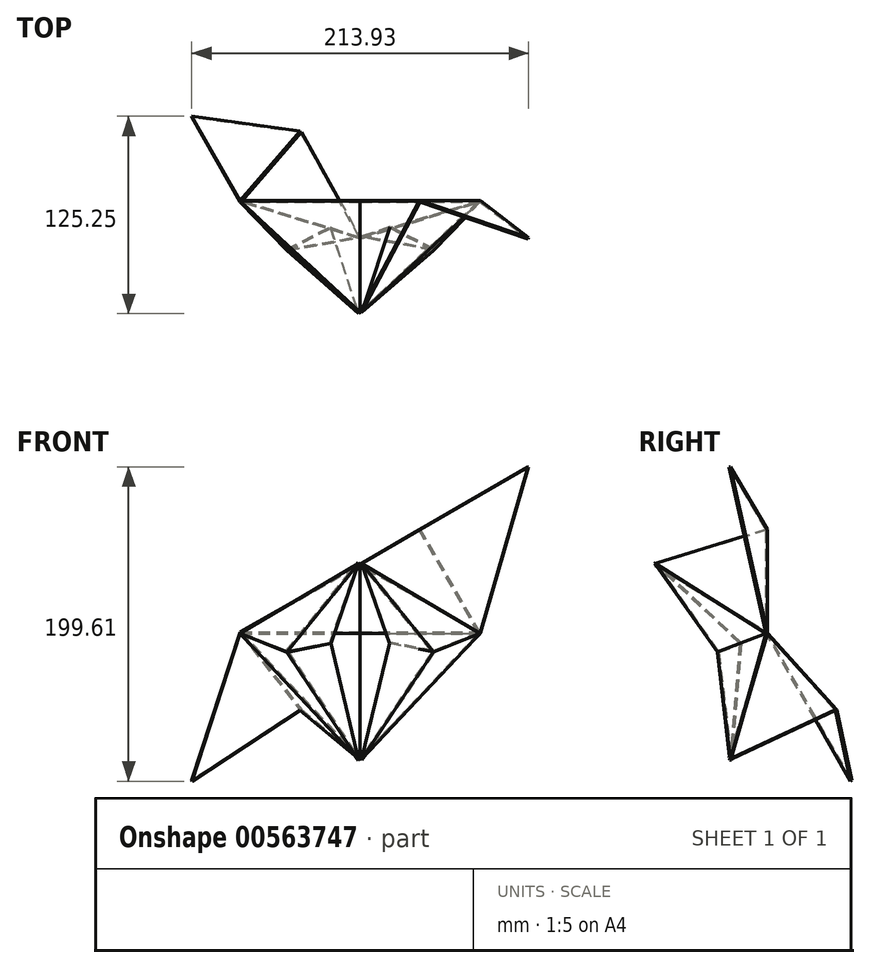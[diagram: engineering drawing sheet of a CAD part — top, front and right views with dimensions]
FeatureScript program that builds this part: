
annotation { "Feature Type Name" : "Feature", "Feature Type Description" : "" }
export const myFeature = defineFeature(function(context is Context, id is Id, definition is map)
    precondition{}
    {
        {
            var Q0;
            Q0=qCreatedBy(makeId("Front.planeOp"),FACE);
            var sketch = newSketch(context, id + "F0", { "sketchPlane" : qUnion([Q0])});
            skLineSegment(sketch, "E0", {"start": v(0, 0) * mm, "end": v(76.2, 0) * mm});
            skLineSegment(sketch, "E1", {"start": v(76.2, 0) * mm, "end": v(152.4, 0) * mm});
            skLineSegment(sketch, "E2", {"start": v(152.4, 0) * mm, "end": v(114.3, 66) * mm});
            skLineSegment(sketch, "E3", {"start": v(0, 0) * mm, "end": v(38.1, 66) * mm});
            skLineSegment(sketch, "E4", {"start": v(38.1, 66) * mm, "end": v(76.2, 131.98) * mm});
            skLineSegment(sketch, "E5", {"start": v(76.2, 131.98) * mm, "end": v(114.3, 66) * mm});
            skLineSegment(sketch, "E6", {"start": v(76.2, 0) * mm, "end": v(76.2, -82.55) * mm});
            skLineSegment(sketch, "E7", {"start": v(38.1, 66) * mm, "end": v(-33.4, 107.27) * mm});
            skLineSegment(sketch, "E8", {"start": v(114.3, 66) * mm, "end": v(185.8, 107.27) * mm});
            skLineSegment(sketch, "E9", {"start": v(-33.4, 107.27) * mm, "end": v(76.2, 131.98) * mm});
            skLineSegment(sketch, "E10", {"start": v(-33.4, 107.27) * mm, "end": v(0, 0) * mm});
            skLineSegment(sketch, "E11", {"start": v(76.2, -82.55) * mm, "end": v(152.4, 0) * mm});
            skLineSegment(sketch, "E12", {"start": v(76.2, -82.55) * mm, "end": v(0, 0) * mm});
            skLineSegment(sketch, "E13", {"start": v(152.4, 0) * mm, "end": v(185.8, 107.27) * mm});
            skLineSegment(sketch, "E14", {"start": v(76.2, 131.98) * mm, "end": v(185.8, 107.27) * mm});
            skLineSegment(sketch, "E15", {"start": v(152.4, 0) * mm, "end": v(189.3, 24.8) * mm});
            skLineSegment(sketch, "E16", {"start": v(189.3, 24.8) * mm, "end": v(185.8, 107.27) * mm});
            skLineSegment(sketch, "E17", {"start": v(152.4, 0) * mm, "end": v(149.38, -44.35) * mm});
            skLineSegment(sketch, "E18", {"start": v(149.38, -44.35) * mm, "end": v(76.2, -82.55) * mm});
            skLineSegment(sketch, "E19", {"start": v(0, 0) * mm, "end": v(3.02, -44.35) * mm});
            skLineSegment(sketch, "E20", {"start": v(3.02, -44.35) * mm, "end": v(76.2, -82.55) * mm});
            skLineSegment(sketch, "E21", {"start": v(0, 0) * mm, "end": v(-36.9, 24.8) * mm});
            skLineSegment(sketch, "E22", {"start": v(-36.9, 24.8) * mm, "end": v(-33.4, 107.27) * mm});
            skLineSegment(sketch, "E23", {"start": v(-33.4, 107.27) * mm, "end": v(36.28, 151.54) * mm});
            skLineSegment(sketch, "E24", {"start": v(36.28, 151.54) * mm, "end": v(76.2, 131.98) * mm});
            skLineSegment(sketch, "E25", {"start": v(76.2, 131.98) * mm, "end": v(116.12, 151.54) * mm});
            skLineSegment(sketch, "E26", {"start": v(116.12, 151.54) * mm, "end": v(185.8, 107.27) * mm});
            skLineSegment(sketch, "E27", {"start": v(149.38, -44.35) * mm, "end": v(152.12, -75.98) * mm});
            skLineSegment(sketch, "E28", {"start": v(152.12, -75.98) * mm, "end": v(76.2, -82.55) * mm});
            skLineSegment(sketch, "E29.MirrorCS", {"start": v(0.28, -75.98) * mm, "end": v(76.2, -82.55) * mm});
            skLineSegment(sketch, "E30.MirrorCS", {"start": v(3.02, -44.35) * mm, "end": v(0.28, -75.98) * mm});
            skLineSegment(sketch, "E31", {"start": v(-36.9, 24.8) * mm, "end": v(-65.66, 38.24) * mm});
            skLineSegment(sketch, "E32", {"start": v(-65.66, 38.24) * mm, "end": v(-33.4, 107.27) * mm});
            skLineSegment(sketch, "E33.MirrorCS", {"start": v(10.26, 169.73) * mm, "end": v(-33.4, 107.27) * mm});
            skLineSegment(sketch, "E34.MirrorCS", {"start": v(36.28, 151.54) * mm, "end": v(10.26, 169.73) * mm});
            skLineSegment(sketch, "E35", {"start": v(116.12, 151.54) * mm, "end": v(142.14, 169.73) * mm});
            skLineSegment(sketch, "E36", {"start": v(142.14, 169.73) * mm, "end": v(185.8, 107.27) * mm});
            skLineSegment(sketch, "E37.MirrorCS", {"start": v(218.06, 38.24) * mm, "end": v(185.8, 107.27) * mm});
            skLineSegment(sketch, "E38.MirrorCS", {"start": v(189.3, 24.8) * mm, "end": v(218.06, 38.24) * mm});
            skText(sketch, "E39", { "text": "angle of 121.5 between three sides of pyramid\nangle of 42 between pyramids (31.5+31.5+42=105)\nangle of 23 of top of star\nangle of 88 of bottom of star\nangle 16.5 of top flap\n", "fontName": "OpenSans-Regular.ttf"});
            skLineSegment(sketch, "E40", {"start": v(76.2, 131.98) * mm, "end": v(76.2, 0) * mm});
            skLineSegment(sketch, "E41", {"start": v(114.3, 66) * mm, "end": v(0, 0) * mm});
            skLineSegment(sketch, "E42", {"start": v(152.4, 0) * mm, "end": v(38.1, 66) * mm});
            skPoint(sketch, "E43", {"position": v(76.2, 44) * mm});
            skPoint(sketch, "E44", {"position": v(76.2, -82.55) * mm});
            skPoint(sketch, "E45", {"position": v(185.8, 107.27) * mm});
            skPoint(sketch, "E46", {"position": v(-33.4, 107.27) * mm});
            skPoint(sketch, "E47", {"position": v(76.2, -44) * mm});
            const initialGuessF0  = {"E39": [0.43458, 0, 1, 0, 0.01522]};
            skSetInitialGuess(sketch, initialGuessF0);
            skSolve(sketch);
        }
        {
            var Q0;
            Q0=makeQuery(id+"F0.imprint","IMPRINT",FACE,{"disambiguationData":[TD([[makeQuery(id+"F0.imprint","IMPRINT",EDGE,{"derivedFrom":sQuery(id+"F0.wireOp",EDGE,"E3")}),1.0]])]});
            var Q1;
            Q1=makeQuery(id+"F0.imprint","IMPRINT",FACE,{"disambiguationData":[TD([[makeQuery(id+"F0.imprint","IMPRINT",EDGE,{"derivedFrom":sQuery(id+"F0.wireOp",EDGE,"E1")}),-1.0]])]});
            var Q2;
            Q2=makeQuery(id+"F0.imprint","IMPRINT",FACE,{"disambiguationData":[TD([[makeQuery(id+"F0.imprint","IMPRINT",EDGE,{"derivedFrom":sQuery(id+"F0.wireOp",EDGE,"E5")}),1.0]])]});
            extrude(context, id + "F1", {"entities" : qUnion([Q0, Q1, Q2]), "depth" : 1.02 * mm, "offsetDistance" : 25.4 * mm});
        }
        {
            var Q0;
            Q0=makeQuery(id+"F0.imprint","IMPRINT",FACE,{"disambiguationData":[TD([[makeQuery(id+"F0.imprint","IMPRINT",EDGE,{"derivedFrom":sQuery(id+"F0.wireOp",EDGE,"E4")}),1.0]])]});
            var Q1;
            Q1=makeQuery(id+"F0.imprint","IMPRINT",FACE,{"disambiguationData":[TD([[makeQuery(id+"F0.imprint","IMPRINT",EDGE,{"derivedFrom":sQuery(id+"F0.wireOp",EDGE,"E0")}),-1.0]])]});
            var Q2;
            Q2=makeQuery(id+"F0.imprint","IMPRINT",FACE,{"disambiguationData":[TD([[makeQuery(id+"F0.imprint","IMPRINT",EDGE,{"derivedFrom":sQuery(id+"F0.wireOp",EDGE,"E2")}),-1.0]])]});
            extrude(context, id + "F2", {"entities" : qUnion([Q0, Q1, Q2]), "depth" : 1.02 * mm, "offsetDistance" : 25.4 * mm});
        }
        {
            var Q0;
            Q0=makeQuery(id+"F0.imprint","IMPRINT",FACE,{"disambiguationData":[TD([[makeQuery(id+"F0.imprint","IMPRINT",EDGE,{"derivedFrom":sQuery(id+"F0.wireOp",EDGE,"E10")}),-1.0]])]});
            var Q1;
            Q1=makeQuery(id+"F0.imprint","IMPRINT",FACE,{"disambiguationData":[TD([[makeQuery(id+"F0.imprint","IMPRINT",EDGE,{"derivedFrom":sQuery(id+"F0.wireOp",EDGE,"E11")}),-1.0]])]});
            var Q2;
            Q2=makeQuery(id+"F0.imprint","IMPRINT",FACE,{"disambiguationData":[TD([[makeQuery(id+"F0.imprint","IMPRINT",EDGE,{"derivedFrom":sQuery(id+"F0.wireOp",EDGE,"E14")}),1.0]])]});
            extrude(context, id + "F3", {"entities" : qUnion([Q0, Q1, Q2]), "depth" : 1.02 * mm, "offsetDistance" : 25.4 * mm});
        }
        {
            var Q0;
            Q0=makeQuery(id+"F0.imprint","IMPRINT",FACE,{"disambiguationData":[TD([[makeQuery(id+"F0.imprint","IMPRINT",EDGE,{"derivedFrom":sQuery(id+"F0.wireOp",EDGE,"E9")}),1.0]])]});
            var Q1;
            Q1=makeQuery(id+"F0.imprint","IMPRINT",FACE,{"disambiguationData":[TD([[makeQuery(id+"F0.imprint","IMPRINT",EDGE,{"derivedFrom":sQuery(id+"F0.wireOp",EDGE,"E12")}),1.0]])]});
            var Q2;
            Q2=makeQuery(id+"F0.imprint","IMPRINT",FACE,{"disambiguationData":[TD([[makeQuery(id+"F0.imprint","IMPRINT",EDGE,{"derivedFrom":sQuery(id+"F0.wireOp",EDGE,"E13")}),-1.0]])]});
            extrude(context, id + "F4", {"entities" : qUnion([Q0, Q1, Q2]), "depth" : 1.02 * mm, "offsetDistance" : 25.4 * mm});
        }
        {
            var Q0;
            Q0=makeQuery(id+"F0.imprint","IMPRINT",FACE,{"disambiguationData":[TD([[makeQuery(id+"F0.imprint","IMPRINT",EDGE,{"derivedFrom":sQuery(id+"F0.wireOp",EDGE,"E22")}),1.0]])]});
            var Q1;
            Q1=makeQuery(id+"F0.imprint","IMPRINT",FACE,{"disambiguationData":[TD([[makeQuery(id+"F0.imprint","IMPRINT",EDGE,{"derivedFrom":sQuery(id+"F0.wireOp",EDGE,"E18")}),1.0]])]});
            var Q2;
            Q2=makeQuery(id+"F0.imprint","IMPRINT",FACE,{"disambiguationData":[TD([[makeQuery(id+"F0.imprint","IMPRINT",EDGE,{"derivedFrom":sQuery(id+"F0.wireOp",EDGE,"E26")}),1.0]])]});
            extrude(context, id + "F5", {"entities" : qUnion([Q0, Q1, Q2]), "depth" : 1.02 * mm, "offsetDistance" : 25.4 * mm});
        }
        {
            var Q0;
            Q0=makeQuery(id+"F0.imprint","IMPRINT",FACE,{"disambiguationData":[TD([[makeQuery(id+"F0.imprint","IMPRINT",EDGE,{"derivedFrom":sQuery(id+"F0.wireOp",EDGE,"E23")}),1.0]])]});
            var Q1;
            Q1=makeQuery(id+"F0.imprint","IMPRINT",FACE,{"disambiguationData":[TD([[makeQuery(id+"F0.imprint","IMPRINT",EDGE,{"derivedFrom":sQuery(id+"F0.wireOp",EDGE,"E20")}),-1.0]])]});
            var Q2;
            Q2=makeQuery(id+"F0.imprint","IMPRINT",FACE,{"disambiguationData":[TD([[makeQuery(id+"F0.imprint","IMPRINT",EDGE,{"derivedFrom":sQuery(id+"F0.wireOp",EDGE,"E16")}),-1.0]])]});
            extrude(context, id + "F6", {"entities" : qUnion([Q0, Q1, Q2]), "depth" : 1.02 * mm, "offsetDistance" : 25.4 * mm});
        }
        {
            var Q0;
            Q0=makeQuery(id+"F2.opExtrude","SWEPT_BODY",BODY,{"disambiguationData":[OSD([sQuery(id+"F0.wireOp",EDGE,"E0"),sQuery(id+"F0.wireOp",EDGE,"E6"),sQuery(id+"F0.wireOp",EDGE,"E12")])]});
            var Q1;
            Q1=makeQuery(id+"F4.opExtrude","SWEPT_BODY",BODY,{"disambiguationData":[OSD([sQuery(id+"F0.wireOp",EDGE,"E12"),sQuery(id+"F0.wireOp",EDGE,"E19"),sQuery(id+"F0.wireOp",EDGE,"E20")])]});
            var Q2;
            Q2=makeQuery(id+"F6.opExtrude","SWEPT_BODY",BODY,{"disambiguationData":[OSD([sQuery(id+"F0.wireOp",EDGE,"E20"),sQuery(id+"F0.wireOp",EDGE,"E29.MirrorCS"),sQuery(id+"F0.wireOp",EDGE,"E30.MirrorCS")])]});
            var Q3;
            Q3=makeQuery(id+"F5.opExtrude","SWEPT_BODY",BODY,{"disambiguationData":[OSD([sQuery(id+"F0.wireOp",EDGE,"E18"),sQuery(id+"F0.wireOp",EDGE,"E27"),sQuery(id+"F0.wireOp",EDGE,"E28")])]});
            var Q4;
            Q4=makeQuery(id+"F3.opExtrude","SWEPT_BODY",BODY,{"disambiguationData":[OSD([sQuery(id+"F0.wireOp",EDGE,"E11"),sQuery(id+"F0.wireOp",EDGE,"E17"),sQuery(id+"F0.wireOp",EDGE,"E18")])]});
            var Q5;
            Q5=makeQuery(id+"F1.opExtrude","SWEPT_BODY",BODY,{"disambiguationData":[OSD([sQuery(id+"F0.wireOp",EDGE,"E1"),sQuery(id+"F0.wireOp",EDGE,"E6"),sQuery(id+"F0.wireOp",EDGE,"E11")])]});
            var Q6;
            Q6=sQuery(id+"F0.wireOp",EDGE,"E1");
            transform(context, id + "F7", {"entities" : qUnion([Q0, Q1, Q2, Q3, Q4, Q5]), "transformType" : TransformType.ROTATION, "transformAxis" : qUnion([Q6]), "angle" : 121.5 * degree, "oppositeDirection" : true, "makeCopy" : false});
        }
        {
            var Q0;
            Q0=makeQuery(id+"F1.opExtrude","SWEPT_BODY",BODY,{"disambiguationData":[OSD([sQuery(id+"F0.wireOp",EDGE,"E3"),sQuery(id+"F0.wireOp",EDGE,"E7"),sQuery(id+"F0.wireOp",EDGE,"E10")])]});
            var Q1;
            Q1=makeQuery(id+"F3.opExtrude","SWEPT_BODY",BODY,{"disambiguationData":[OSD([sQuery(id+"F0.wireOp",EDGE,"E10"),sQuery(id+"F0.wireOp",EDGE,"E21"),sQuery(id+"F0.wireOp",EDGE,"E22")])]});
            var Q2;
            Q2=makeQuery(id+"F5.opExtrude","SWEPT_BODY",BODY,{"disambiguationData":[OSD([sQuery(id+"F0.wireOp",EDGE,"E22"),sQuery(id+"F0.wireOp",EDGE,"E31"),sQuery(id+"F0.wireOp",EDGE,"E32")])]});
            var Q3;
            Q3=makeQuery(id+"F6.opExtrude","SWEPT_BODY",BODY,{"disambiguationData":[OSD([sQuery(id+"F0.wireOp",EDGE,"E23"),sQuery(id+"F0.wireOp",EDGE,"E33.MirrorCS"),sQuery(id+"F0.wireOp",EDGE,"E34.MirrorCS")])]});
            var Q4;
            Q4=makeQuery(id+"F4.opExtrude","SWEPT_BODY",BODY,{"disambiguationData":[OSD([sQuery(id+"F0.wireOp",EDGE,"E9"),sQuery(id+"F0.wireOp",EDGE,"E23"),sQuery(id+"F0.wireOp",EDGE,"E24")])]});
            var Q5;
            Q5=makeQuery(id+"F2.opExtrude","SWEPT_BODY",BODY,{"disambiguationData":[OSD([sQuery(id+"F0.wireOp",EDGE,"E4"),sQuery(id+"F0.wireOp",EDGE,"E7"),sQuery(id+"F0.wireOp",EDGE,"E9")])]});
            var Q6;
            Q6=sQuery(id+"F0.wireOp",EDGE,"E3");
            transform(context, id + "F8", {"entities" : qUnion([Q0, Q1, Q2, Q3, Q4, Q5]), "transformType" : TransformType.ROTATION, "transformAxis" : qUnion([Q6]), "angle" : 121.5 * degree, "makeCopy" : false});
        }
        {
            var Q0;
            Q0=makeQuery(id+"F2.opExtrude","SWEPT_BODY",BODY,{"disambiguationData":[OSD([sQuery(id+"F0.wireOp",EDGE,"E2"),sQuery(id+"F0.wireOp",EDGE,"E8"),sQuery(id+"F0.wireOp",EDGE,"E13")])]});
            var Q1;
            Q1=makeQuery(id+"F1.opExtrude","SWEPT_BODY",BODY,{"disambiguationData":[OSD([sQuery(id+"F0.wireOp",EDGE,"E5"),sQuery(id+"F0.wireOp",EDGE,"E8"),sQuery(id+"F0.wireOp",EDGE,"E14")])]});
            var Q2;
            Q2=makeQuery(id+"F3.opExtrude","SWEPT_BODY",BODY,{"disambiguationData":[OSD([sQuery(id+"F0.wireOp",EDGE,"E14"),sQuery(id+"F0.wireOp",EDGE,"E25"),sQuery(id+"F0.wireOp",EDGE,"E26")])]});
            var Q3;
            Q3=makeQuery(id+"F5.opExtrude","SWEPT_BODY",BODY,{"disambiguationData":[OSD([sQuery(id+"F0.wireOp",EDGE,"E26"),sQuery(id+"F0.wireOp",EDGE,"E35"),sQuery(id+"F0.wireOp",EDGE,"E36")])]});
            var Q4;
            Q4=makeQuery(id+"F6.opExtrude","SWEPT_BODY",BODY,{"disambiguationData":[OSD([sQuery(id+"F0.wireOp",EDGE,"E16"),sQuery(id+"F0.wireOp",EDGE,"E37.MirrorCS"),sQuery(id+"F0.wireOp",EDGE,"E38.MirrorCS")])]});
            var Q5;
            Q5=makeQuery(id+"F4.opExtrude","SWEPT_BODY",BODY,{"disambiguationData":[OSD([sQuery(id+"F0.wireOp",EDGE,"E13"),sQuery(id+"F0.wireOp",EDGE,"E15"),sQuery(id+"F0.wireOp",EDGE,"E16")])]});
            var Q6;
            Q6=sQuery(id+"F0.wireOp",EDGE,"E5");
            transform(context, id + "F9", {"entities" : qUnion([Q0, Q1, Q2, Q3, Q4, Q5]), "transformType" : TransformType.ROTATION, "transformAxis" : qUnion([Q6]), "angle" : 121.5 * degree, "makeCopy" : false});
        }
        {
            var Q0;
            Q0=makeQuery(id+"F4.opExtrude","SWEPT_BODY",BODY,{"disambiguationData":[OSD([sQuery(id+"F0.wireOp",EDGE,"E13"),sQuery(id+"F0.wireOp",EDGE,"E15"),sQuery(id+"F0.wireOp",EDGE,"E16")])]});
            var Q1;
            Q1=makeQuery(id+"F6.opExtrude","SWEPT_BODY",BODY,{"disambiguationData":[OSD([sQuery(id+"F0.wireOp",EDGE,"E16"),sQuery(id+"F0.wireOp",EDGE,"E37.MirrorCS"),sQuery(id+"F0.wireOp",EDGE,"E38.MirrorCS")])]});
            var Q2;
            Q2=makeQuery(id+"F2.opExtrude","CAP_EDGE",EDGE,{"disambiguationData":[OSD([sQuery(id+"F0.wireOp",EDGE,"E13")])],"isStart":true});
            transform(context, id + "F10", {"entities" : qUnion([Q0, Q1]), "transformType" : TransformType.ROTATION, "transformAxis" : qUnion([Q2]), "angle" : 23 * degree, "oppositeDirection" : true, "makeCopy" : false});
        }
        {
            var Q0;
            Q0=makeQuery(id+"F3.opExtrude","SWEPT_BODY",BODY,{"disambiguationData":[OSD([sQuery(id+"F0.wireOp",EDGE,"E11"),sQuery(id+"F0.wireOp",EDGE,"E17"),sQuery(id+"F0.wireOp",EDGE,"E18")])]});
            var Q1;
            Q1=makeQuery(id+"F5.opExtrude","SWEPT_BODY",BODY,{"disambiguationData":[OSD([sQuery(id+"F0.wireOp",EDGE,"E18"),sQuery(id+"F0.wireOp",EDGE,"E27"),sQuery(id+"F0.wireOp",EDGE,"E28")])]});
            var Q2;
            Q2=makeQuery(id+"F1.opExtrude","CAP_EDGE",EDGE,{"disambiguationData":[OSD([sQuery(id+"F0.wireOp",EDGE,"E11")])],"isStart":true});
            transform(context, id + "F11", {"entities" : qUnion([Q0, Q1]), "transformType" : TransformType.ROTATION, "transformAxis" : qUnion([Q2]), "angle" : 23 * degree, "oppositeDirection" : true, "makeCopy" : false});
        }
        {
            var Q0;
            Q0=makeQuery(id+"F4.opExtrude","SWEPT_BODY",BODY,{"disambiguationData":[OSD([sQuery(id+"F0.wireOp",EDGE,"E9"),sQuery(id+"F0.wireOp",EDGE,"E23"),sQuery(id+"F0.wireOp",EDGE,"E24")])]});
            var Q1;
            Q1=makeQuery(id+"F6.opExtrude","SWEPT_BODY",BODY,{"disambiguationData":[OSD([sQuery(id+"F0.wireOp",EDGE,"E23"),sQuery(id+"F0.wireOp",EDGE,"E33.MirrorCS"),sQuery(id+"F0.wireOp",EDGE,"E34.MirrorCS")])]});
            var Q2;
            Q2=makeQuery(id+"F2.opExtrude","CAP_EDGE",EDGE,{"disambiguationData":[OSD([sQuery(id+"F0.wireOp",EDGE,"E9")])],"isStart":true});
            transform(context, id + "F12", {"entities" : qUnion([Q0, Q1]), "transformType" : TransformType.ROTATION, "transformAxis" : qUnion([Q2]), "angle" : 23 * degree, "makeCopy" : false});
        }
        {
            var Q0;
            Q0=makeQuery(id+"F3.opExtrude","SWEPT_BODY",BODY,{"disambiguationData":[OSD([sQuery(id+"F0.wireOp",EDGE,"E14"),sQuery(id+"F0.wireOp",EDGE,"E25"),sQuery(id+"F0.wireOp",EDGE,"E26")])]});
            var Q1;
            Q1=makeQuery(id+"F5.opExtrude","SWEPT_BODY",BODY,{"disambiguationData":[OSD([sQuery(id+"F0.wireOp",EDGE,"E26"),sQuery(id+"F0.wireOp",EDGE,"E35"),sQuery(id+"F0.wireOp",EDGE,"E36")])]});
            var Q2;
            Q2=makeQuery(id+"F1.opExtrude","CAP_EDGE",EDGE,{"disambiguationData":[OSD([sQuery(id+"F0.wireOp",EDGE,"E14")])],"isStart":true});
            transform(context, id + "F13", {"entities" : qUnion([Q0, Q1]), "transformType" : TransformType.ROTATION, "transformAxis" : qUnion([Q2]), "angle" : 23 * degree, "makeCopy" : false});
        }
        {
            var Q0;
            Q0=makeQuery(id+"F4.opExtrude","SWEPT_BODY",BODY,{"disambiguationData":[OSD([sQuery(id+"F0.wireOp",EDGE,"E12"),sQuery(id+"F0.wireOp",EDGE,"E19"),sQuery(id+"F0.wireOp",EDGE,"E20")])]});
            var Q1;
            Q1=makeQuery(id+"F6.opExtrude","SWEPT_BODY",BODY,{"disambiguationData":[OSD([sQuery(id+"F0.wireOp",EDGE,"E20"),sQuery(id+"F0.wireOp",EDGE,"E29.MirrorCS"),sQuery(id+"F0.wireOp",EDGE,"E30.MirrorCS")])]});
            var Q2;
            Q2=makeQuery(id+"F1.opExtrude","CAP_EDGE",EDGE,{"disambiguationData":[OSD([sQuery(id+"F0.wireOp",EDGE,"E10")])],"isStart":true});
            transform(context, id + "F14", {"entities" : qUnion([Q0, Q1]), "transformType" : TransformType.ROTATION, "transformAxis" : qUnion([Q2]), "angle" : 23 * degree, "makeCopy" : false});
        }
        {
            var Q0;
            Q0=makeQuery(id+"F3.opExtrude","SWEPT_BODY",BODY,{"disambiguationData":[OSD([sQuery(id+"F0.wireOp",EDGE,"E10"),sQuery(id+"F0.wireOp",EDGE,"E21"),sQuery(id+"F0.wireOp",EDGE,"E22")])]});
            var Q1;
            Q1=makeQuery(id+"F5.opExtrude","SWEPT_BODY",BODY,{"disambiguationData":[OSD([sQuery(id+"F0.wireOp",EDGE,"E22"),sQuery(id+"F0.wireOp",EDGE,"E31"),sQuery(id+"F0.wireOp",EDGE,"E32")])]});
            var Q2;
            Q2=makeQuery(id+"F4.opExtrude","CAP_EDGE",EDGE,{"disambiguationData":[OSD([sQuery(id+"F0.wireOp",EDGE,"E12")])],"isStart":true});
            transform(context, id + "F15", {"entities" : qUnion([Q0, Q1]), "transformType" : TransformType.ROTATION, "transformAxis" : qUnion([Q2]), "angle" : 23 * degree, "oppositeDirection" : true, "makeCopy" : false});
        }
        {
            var Q0;
            Q0=makeQuery(id+"F6.opExtrude","SWEPT_BODY",BODY,{"disambiguationData":[OSD([sQuery(id+"F0.wireOp",EDGE,"E23"),sQuery(id+"F0.wireOp",EDGE,"E33.MirrorCS"),sQuery(id+"F0.wireOp",EDGE,"E34.MirrorCS")])]});
            var Q1;
            Q1=makeQuery(id+"F4.opExtrude","CAP_EDGE",EDGE,{"disambiguationData":[OSD([sQuery(id+"F0.wireOp",EDGE,"E23")])],"isStart":true});
            transform(context, id + "F16", {"entities" : qUnion([Q0]), "transformType" : TransformType.ROTATION, "transformAxis" : qUnion([Q1]), "angle" : 88 * degree, "makeCopy" : false});
        }
        {
            var Q0;
            Q0=makeQuery(id+"F5.opExtrude","SWEPT_BODY",BODY,{"disambiguationData":[OSD([sQuery(id+"F0.wireOp",EDGE,"E18"),sQuery(id+"F0.wireOp",EDGE,"E27"),sQuery(id+"F0.wireOp",EDGE,"E28")])]});
            var Q1;
            Q1=makeQuery(id+"F3.opExtrude","CAP_EDGE",EDGE,{"disambiguationData":[OSD([sQuery(id+"F0.wireOp",EDGE,"E18")])],"isStart":true});
            transform(context, id + "F17", {"entities" : qUnion([Q0]), "transformType" : TransformType.ROTATION, "transformAxis" : qUnion([Q1]), "angle" : 88 * degree, "makeCopy" : false});
        }
        {
            var Q0;
            Q0=makeQuery(id+"F6.opExtrude","SWEPT_BODY",BODY,{"disambiguationData":[OSD([sQuery(id+"F0.wireOp",EDGE,"E16"),sQuery(id+"F0.wireOp",EDGE,"E37.MirrorCS"),sQuery(id+"F0.wireOp",EDGE,"E38.MirrorCS")])]});
            var Q1;
            Q1=makeQuery(id+"F4.opExtrude","CAP_EDGE",EDGE,{"disambiguationData":[OSD([sQuery(id+"F0.wireOp",EDGE,"E16")])],"isStart":true});
            transform(context, id + "F18", {"entities" : qUnion([Q0]), "transformType" : TransformType.ROTATION, "transformAxis" : qUnion([Q1]), "angle" : 88 * degree, "oppositeDirection" : true, "makeCopy" : false});
        }
        {
            var Q0;
            Q0=makeQuery(id+"F5.opExtrude","SWEPT_BODY",BODY,{"disambiguationData":[OSD([sQuery(id+"F0.wireOp",EDGE,"E22"),sQuery(id+"F0.wireOp",EDGE,"E31"),sQuery(id+"F0.wireOp",EDGE,"E32")])]});
            var Q1;
            Q1=makeQuery(id+"F3.opExtrude","CAP_EDGE",EDGE,{"disambiguationData":[OSD([sQuery(id+"F0.wireOp",EDGE,"E22")])],"isStart":true});
            transform(context, id + "F19", {"entities" : qUnion([Q0]), "transformType" : TransformType.ROTATION, "transformAxis" : qUnion([Q1]), "angle" : 88 * degree, "makeCopy" : false});
        }
        {
            var Q0;
            Q0=makeQuery(id+"F6.opExtrude","SWEPT_BODY",BODY,{"disambiguationData":[OSD([sQuery(id+"F0.wireOp",EDGE,"E20"),sQuery(id+"F0.wireOp",EDGE,"E29.MirrorCS"),sQuery(id+"F0.wireOp",EDGE,"E30.MirrorCS")])]});
            var Q1;
            Q1=makeQuery(id+"F4.opExtrude","CAP_EDGE",EDGE,{"disambiguationData":[OSD([sQuery(id+"F0.wireOp",EDGE,"E20")])],"isStart":true});
            transform(context, id + "F20", {"entities" : qUnion([Q0]), "transformType" : TransformType.ROTATION, "transformAxis" : qUnion([Q1]), "angle" : 88 * degree, "oppositeDirection" : true, "makeCopy" : false});
        }
        {
            var Q0;
            Q0=makeQuery(id+"F5.opExtrude","SWEPT_BODY",BODY,{"disambiguationData":[OSD([sQuery(id+"F0.wireOp",EDGE,"E26"),sQuery(id+"F0.wireOp",EDGE,"E35"),sQuery(id+"F0.wireOp",EDGE,"E36")])]});
            var Q1;
            Q1=makeQuery(id+"F3.opExtrude","CAP_EDGE",EDGE,{"disambiguationData":[OSD([sQuery(id+"F0.wireOp",EDGE,"E26")])],"isStart":true});
            transform(context, id + "F21", {"entities" : qUnion([Q0]), "transformType" : TransformType.ROTATION, "transformAxis" : qUnion([Q1]), "angle" : 88 * degree, "makeCopy" : false});
        }
        {
            var Q0;
            Q0=makeQuery(id+"F5.opExtrude","SWEPT_BODY",BODY,{"disambiguationData":[OSD([sQuery(id+"F0.wireOp",EDGE,"E22"),sQuery(id+"F0.wireOp",EDGE,"E31"),sQuery(id+"F0.wireOp",EDGE,"E32")])]});
            var Q1;
            Q1=makeQuery(id+"F5.opExtrude","SWEPT_BODY",BODY,{"disambiguationData":[OSD([sQuery(id+"F0.wireOp",EDGE,"E18"),sQuery(id+"F0.wireOp",EDGE,"E27"),sQuery(id+"F0.wireOp",EDGE,"E28")])]});
            var Q2;
            Q2=makeQuery(id+"F5.opExtrude","SWEPT_BODY",BODY,{"disambiguationData":[OSD([sQuery(id+"F0.wireOp",EDGE,"E26"),sQuery(id+"F0.wireOp",EDGE,"E35"),sQuery(id+"F0.wireOp",EDGE,"E36")])]});
            var Q3;
            Q3=makeQuery(id+"F6.opExtrude","SWEPT_BODY",BODY,{"disambiguationData":[OSD([sQuery(id+"F0.wireOp",EDGE,"E23"),sQuery(id+"F0.wireOp",EDGE,"E33.MirrorCS"),sQuery(id+"F0.wireOp",EDGE,"E34.MirrorCS")])]});
            var Q4;
            Q4=makeQuery(id+"F6.opExtrude","SWEPT_BODY",BODY,{"disambiguationData":[OSD([sQuery(id+"F0.wireOp",EDGE,"E16"),sQuery(id+"F0.wireOp",EDGE,"E37.MirrorCS"),sQuery(id+"F0.wireOp",EDGE,"E38.MirrorCS")])]});
            var Q5;
            Q5=makeQuery(id+"F6.opExtrude","SWEPT_BODY",BODY,{"disambiguationData":[OSD([sQuery(id+"F0.wireOp",EDGE,"E20"),sQuery(id+"F0.wireOp",EDGE,"E29.MirrorCS"),sQuery(id+"F0.wireOp",EDGE,"E30.MirrorCS")])]});
            var Q6;
            Q6=makeQuery(id+"F4.opExtrude","SWEPT_BODY",BODY,{"disambiguationData":[OSD([sQuery(id+"F0.wireOp",EDGE,"E12"),sQuery(id+"F0.wireOp",EDGE,"E19"),sQuery(id+"F0.wireOp",EDGE,"E20")])]});
            var Q7;
            Q7=makeQuery(id+"F4.opExtrude","SWEPT_BODY",BODY,{"disambiguationData":[OSD([sQuery(id+"F0.wireOp",EDGE,"E13"),sQuery(id+"F0.wireOp",EDGE,"E15"),sQuery(id+"F0.wireOp",EDGE,"E16")])]});
            var Q8;
            Q8=makeQuery(id+"F4.opExtrude","SWEPT_BODY",BODY,{"disambiguationData":[OSD([sQuery(id+"F0.wireOp",EDGE,"E9"),sQuery(id+"F0.wireOp",EDGE,"E23"),sQuery(id+"F0.wireOp",EDGE,"E24")])]});
            var Q9;
            Q9=makeQuery(id+"F3.opExtrude","SWEPT_BODY",BODY,{"disambiguationData":[OSD([sQuery(id+"F0.wireOp",EDGE,"E11"),sQuery(id+"F0.wireOp",EDGE,"E17"),sQuery(id+"F0.wireOp",EDGE,"E18")])]});
            var Q10;
            Q10=makeQuery(id+"F3.opExtrude","SWEPT_BODY",BODY,{"disambiguationData":[OSD([sQuery(id+"F0.wireOp",EDGE,"E10"),sQuery(id+"F0.wireOp",EDGE,"E21"),sQuery(id+"F0.wireOp",EDGE,"E22")])]});
            var Q11;
            Q11=makeQuery(id+"F3.opExtrude","SWEPT_BODY",BODY,{"disambiguationData":[OSD([sQuery(id+"F0.wireOp",EDGE,"E14"),sQuery(id+"F0.wireOp",EDGE,"E25"),sQuery(id+"F0.wireOp",EDGE,"E26")])]});
            var Q12;
            Q12=makeQuery(id+"F2.opExtrude","SWEPT_BODY",BODY,{"disambiguationData":[OSD([sQuery(id+"F0.wireOp",EDGE,"E4"),sQuery(id+"F0.wireOp",EDGE,"E7"),sQuery(id+"F0.wireOp",EDGE,"E9")])]});
            var Q13;
            Q13=makeQuery(id+"F2.opExtrude","SWEPT_BODY",BODY,{"disambiguationData":[OSD([sQuery(id+"F0.wireOp",EDGE,"E2"),sQuery(id+"F0.wireOp",EDGE,"E8"),sQuery(id+"F0.wireOp",EDGE,"E13")])]});
            var Q14;
            Q14=makeQuery(id+"F2.opExtrude","SWEPT_BODY",BODY,{"disambiguationData":[OSD([sQuery(id+"F0.wireOp",EDGE,"E0"),sQuery(id+"F0.wireOp",EDGE,"E6"),sQuery(id+"F0.wireOp",EDGE,"E12")])]});
            var Q15;
            Q15=makeQuery(id+"F1.opExtrude","SWEPT_BODY",BODY,{"disambiguationData":[OSD([sQuery(id+"F0.wireOp",EDGE,"E5"),sQuery(id+"F0.wireOp",EDGE,"E8"),sQuery(id+"F0.wireOp",EDGE,"E14")])]});
            var Q16;
            Q16=makeQuery(id+"F1.opExtrude","SWEPT_BODY",BODY,{"disambiguationData":[OSD([sQuery(id+"F0.wireOp",EDGE,"E3"),sQuery(id+"F0.wireOp",EDGE,"E7"),sQuery(id+"F0.wireOp",EDGE,"E10")])]});
            var Q17;
            Q17=makeQuery(id+"F1.opExtrude","SWEPT_BODY",BODY,{"disambiguationData":[OSD([sQuery(id+"F0.wireOp",EDGE,"E1"),sQuery(id+"F0.wireOp",EDGE,"E6"),sQuery(id+"F0.wireOp",EDGE,"E11")])]});
            var Q18;
            Q18=qCreatedBy(makeId("Top.planeOp"),FACE);
            mirror(context, id + "F22", {"entities" : qUnion([Q0, Q1, Q2, Q3, Q4, Q5, Q6, Q7, Q8, Q9, Q10, Q11, Q12, Q13, Q14, Q15, Q16, Q17]), "mirrorPlane" : qUnion([Q18])});
        }
        {
            var Q0;
            Q0=makeQuery(id+"F22.opPattern","COPY",BODY,{"derivedFrom":makeQuery(id+"F2.opExtrude","SWEPT_BODY",BODY,{"disambiguationData":[OSD([sQuery(id+"F0.wireOp",EDGE,"E4"),sQuery(id+"F0.wireOp",EDGE,"E7"),sQuery(id+"F0.wireOp",EDGE,"E9")])]}),"instanceName":"1"});
            var Q1;
            Q1=makeQuery(id+"F22.opPattern","COPY",BODY,{"derivedFrom":makeQuery(id+"F2.opExtrude","SWEPT_BODY",BODY,{"disambiguationData":[OSD([sQuery(id+"F0.wireOp",EDGE,"E0"),sQuery(id+"F0.wireOp",EDGE,"E6"),sQuery(id+"F0.wireOp",EDGE,"E12")])]}),"instanceName":"1"});
            var Q2;
            Q2=makeQuery(id+"F22.opPattern","COPY",BODY,{"derivedFrom":makeQuery(id+"F3.opExtrude","SWEPT_BODY",BODY,{"disambiguationData":[OSD([sQuery(id+"F0.wireOp",EDGE,"E10"),sQuery(id+"F0.wireOp",EDGE,"E21"),sQuery(id+"F0.wireOp",EDGE,"E22")])]}),"instanceName":"1"});
            var Q3;
            Q3=makeQuery(id+"F22.opPattern","COPY",BODY,{"derivedFrom":makeQuery(id+"F2.opExtrude","SWEPT_BODY",BODY,{"disambiguationData":[OSD([sQuery(id+"F0.wireOp",EDGE,"E2"),sQuery(id+"F0.wireOp",EDGE,"E8"),sQuery(id+"F0.wireOp",EDGE,"E13")])]}),"instanceName":"1"});
            var Q4;
            Q4=makeQuery(id+"F22.opPattern","COPY",BODY,{"derivedFrom":makeQuery(id+"F1.opExtrude","SWEPT_BODY",BODY,{"disambiguationData":[OSD([sQuery(id+"F0.wireOp",EDGE,"E5"),sQuery(id+"F0.wireOp",EDGE,"E8"),sQuery(id+"F0.wireOp",EDGE,"E14")])]}),"instanceName":"1"});
            var Q5;
            Q5=makeQuery(id+"F22.opPattern","COPY",BODY,{"derivedFrom":makeQuery(id+"F1.opExtrude","SWEPT_BODY",BODY,{"disambiguationData":[OSD([sQuery(id+"F0.wireOp",EDGE,"E3"),sQuery(id+"F0.wireOp",EDGE,"E7"),sQuery(id+"F0.wireOp",EDGE,"E10")])]}),"instanceName":"1"});
            var Q6;
            Q6=makeQuery(id+"F22.opPattern","COPY",BODY,{"derivedFrom":makeQuery(id+"F1.opExtrude","SWEPT_BODY",BODY,{"disambiguationData":[OSD([sQuery(id+"F0.wireOp",EDGE,"E1"),sQuery(id+"F0.wireOp",EDGE,"E6"),sQuery(id+"F0.wireOp",EDGE,"E11")])]}),"instanceName":"1"});
            var Q7;
            Q7=makeQuery(id+"F22.opPattern","COPY",BODY,{"derivedFrom":makeQuery(id+"F6.opExtrude","SWEPT_BODY",BODY,{"disambiguationData":[OSD([sQuery(id+"F0.wireOp",EDGE,"E23"),sQuery(id+"F0.wireOp",EDGE,"E33.MirrorCS"),sQuery(id+"F0.wireOp",EDGE,"E34.MirrorCS")])]}),"instanceName":"1"});
            var Q8;
            Q8=makeQuery(id+"F22.opPattern","COPY",BODY,{"derivedFrom":makeQuery(id+"F3.opExtrude","SWEPT_BODY",BODY,{"disambiguationData":[OSD([sQuery(id+"F0.wireOp",EDGE,"E14"),sQuery(id+"F0.wireOp",EDGE,"E25"),sQuery(id+"F0.wireOp",EDGE,"E26")])]}),"instanceName":"1"});
            var Q9;
            Q9=makeQuery(id+"F22.opPattern","COPY",BODY,{"derivedFrom":makeQuery(id+"F4.opExtrude","SWEPT_BODY",BODY,{"disambiguationData":[OSD([sQuery(id+"F0.wireOp",EDGE,"E12"),sQuery(id+"F0.wireOp",EDGE,"E19"),sQuery(id+"F0.wireOp",EDGE,"E20")])]}),"instanceName":"1"});
            var Q10;
            Q10=makeQuery(id+"F22.opPattern","COPY",BODY,{"derivedFrom":makeQuery(id+"F3.opExtrude","SWEPT_BODY",BODY,{"disambiguationData":[OSD([sQuery(id+"F0.wireOp",EDGE,"E11"),sQuery(id+"F0.wireOp",EDGE,"E17"),sQuery(id+"F0.wireOp",EDGE,"E18")])]}),"instanceName":"1"});
            var Q11;
            Q11=makeQuery(id+"F22.opPattern","COPY",BODY,{"derivedFrom":makeQuery(id+"F4.opExtrude","SWEPT_BODY",BODY,{"disambiguationData":[OSD([sQuery(id+"F0.wireOp",EDGE,"E9"),sQuery(id+"F0.wireOp",EDGE,"E23"),sQuery(id+"F0.wireOp",EDGE,"E24")])]}),"instanceName":"1"});
            var Q12;
            Q12=makeQuery(id+"F22.opPattern","COPY",BODY,{"derivedFrom":makeQuery(id+"F5.opExtrude","SWEPT_BODY",BODY,{"disambiguationData":[OSD([sQuery(id+"F0.wireOp",EDGE,"E18"),sQuery(id+"F0.wireOp",EDGE,"E27"),sQuery(id+"F0.wireOp",EDGE,"E28")])]}),"instanceName":"1"});
            var Q13;
            Q13=makeQuery(id+"F22.opPattern","COPY",BODY,{"derivedFrom":makeQuery(id+"F4.opExtrude","SWEPT_BODY",BODY,{"disambiguationData":[OSD([sQuery(id+"F0.wireOp",EDGE,"E13"),sQuery(id+"F0.wireOp",EDGE,"E15"),sQuery(id+"F0.wireOp",EDGE,"E16")])]}),"instanceName":"1"});
            var Q14;
            Q14=makeQuery(id+"F22.opPattern","COPY",BODY,{"derivedFrom":makeQuery(id+"F5.opExtrude","SWEPT_BODY",BODY,{"disambiguationData":[OSD([sQuery(id+"F0.wireOp",EDGE,"E22"),sQuery(id+"F0.wireOp",EDGE,"E31"),sQuery(id+"F0.wireOp",EDGE,"E32")])]}),"instanceName":"1"});
            var Q15;
            Q15=makeQuery(id+"F22.opPattern","COPY",BODY,{"derivedFrom":makeQuery(id+"F6.opExtrude","SWEPT_BODY",BODY,{"disambiguationData":[OSD([sQuery(id+"F0.wireOp",EDGE,"E16"),sQuery(id+"F0.wireOp",EDGE,"E37.MirrorCS"),sQuery(id+"F0.wireOp",EDGE,"E38.MirrorCS")])]}),"instanceName":"1"});
            var Q16;
            Q16=makeQuery(id+"F22.opPattern","COPY",BODY,{"derivedFrom":makeQuery(id+"F5.opExtrude","SWEPT_BODY",BODY,{"disambiguationData":[OSD([sQuery(id+"F0.wireOp",EDGE,"E26"),sQuery(id+"F0.wireOp",EDGE,"E35"),sQuery(id+"F0.wireOp",EDGE,"E36")])]}),"instanceName":"1"});
            var Q17;
            Q17=makeQuery(id+"F22.opPattern","COPY",BODY,{"derivedFrom":makeQuery(id+"F6.opExtrude","SWEPT_BODY",BODY,{"disambiguationData":[OSD([sQuery(id+"F0.wireOp",EDGE,"E20"),sQuery(id+"F0.wireOp",EDGE,"E29.MirrorCS"),sQuery(id+"F0.wireOp",EDGE,"E30.MirrorCS")])]}),"instanceName":"1"});
            var Q18;
            Q18=sQuery(id+"F0.wireOp",EDGE,"E1");
            transform(context, id + "F23", {"entities" : qUnion([Q0, Q1, Q2, Q3, Q4, Q5, Q6, Q7, Q8, Q9, Q10, Q11, Q12, Q13, Q14, Q15, Q16, Q17]), "transformType" : TransformType.ROTATION, "transformAxis" : qUnion([Q18]), "angle" : 42 * degree, "makeCopy" : false});
        }
        {
            var Q0;
            Q0=makeQuery(id+"F0.imprint","IMPRINT",FACE,{"disambiguationData":[TD([[makeQuery(id+"F0.imprint","IMPRINT",EDGE,{"derivedFrom":sQuery(id+"F0.wireOp",EDGE,"E2")}),-1.0]])]});
            extrude(context, id + "F24", {"entities" : qUnion([Q0]), "oppositeDirection" : true, "depth" : 1.02 * mm, "offsetDistance" : 25.4 * mm});
        }
        {
            var Q0;
            Q0=makeQuery(id+"F24.opExtrude","SWEPT_BODY",BODY,{"disambiguationData":[OSD([sQuery(id+"F0.wireOp",EDGE,"E2"),sQuery(id+"F0.wireOp",EDGE,"E8"),sQuery(id+"F0.wireOp",EDGE,"E13")])]});
            var Q1;
            Q1=sQuery(id+"F0.wireOp",EDGE,"E2");
            transform(context, id + "F25", {"entities" : qUnion([Q0]), "transformType" : TransformType.ROTATION, "transformAxis" : qUnion([Q1]), "angle" : 16.5 * degree, "oppositeDirection" : true, "makeCopy" : false});
        }
        {
            var Q0;
            Q0=makeQuery(id+"F22.opPattern","COPY",VERTEX,{"derivedFrom":makeQuery(id+"F4.opExtrude","CAP_VERTEX",VERTEX,{"disambiguationData":[OSD([sQuery(id+"F0.wireOp",EDGE,"E4"),sQuery(id+"F0.wireOp",EDGE,"E5"),sQuery(id+"F0.wireOp",EDGE,"E9"),sQuery(id+"F0.wireOp",EDGE,"E14"),sQuery(id+"F0.wireOp",EDGE,"E24"),sQuery(id+"F0.wireOp",EDGE,"E25")])],"isStart":false}),"instanceName":"1"});
            var Q1;
            Q1=sQuery(id+"F0.wireOp",VERTEX,"E12.end");
            var Q2;
            Q2=sQuery(id+"F0.wireOp",VERTEX,"E11.end");
            cPlane(context, id + "F26", {"entities" : qUnion([Q0, Q1, Q2]), "cplaneType" : CPlaneType.THREE_POINT, "offset" : 25.4 * mm, "width" : 152.4 * mm, "height" : 152.4 * mm});
        }
        {
            var Q0;
            Q0=qCreatedBy(id+"F26.planeOp",FACE);
            var Q1;
            Q1=makeQuery(id+"F22.opPattern","COPY",EDGE,{"derivedFrom":makeQuery(id+"F2.opExtrude","CAP_EDGE",EDGE,{"disambiguationData":[OSD([sQuery(id+"F0.wireOp",EDGE,"E4")])],"isStart":true}),"instanceName":"1"});
            cPlane(context, id + "F27", {"entities" : qUnion([Q0, Q1]), "cplaneType" : CPlaneType.LINE_ANGLE, "offset" : 25.4 * mm, "angle" : 90 * degree, "width" : 152.4 * mm, "height" : 152.4 * mm});
        }
        {
            var Q0;
            Q0=makeQuery(id+"F22.opPattern","COPY",BODY,{"derivedFrom":makeQuery(id+"F1.opExtrude","SWEPT_BODY",BODY,{"disambiguationData":[OSD([sQuery(id+"F0.wireOp",EDGE,"E3"),sQuery(id+"F0.wireOp",EDGE,"E7"),sQuery(id+"F0.wireOp",EDGE,"E10")])]}),"instanceName":"1"});
            var Q1;
            Q1=qCreatedBy(id+"F27.planeOp",FACE);
            mirror(context, id + "F28", {"entities" : qUnion([Q0]), "mirrorPlane" : qUnion([Q1])});
        }
        {
            var Q0;
            Q0=makeQuery(id+"F28.opPattern","COPY",BODY,{"derivedFrom":makeQuery(id+"F22.opPattern","COPY",BODY,{"derivedFrom":makeQuery(id+"F1.opExtrude","SWEPT_BODY",BODY,{"disambiguationData":[OSD([sQuery(id+"F0.wireOp",EDGE,"E3"),sQuery(id+"F0.wireOp",EDGE,"E7"),sQuery(id+"F0.wireOp",EDGE,"E10")])]}),"instanceName":"1"}),"instanceName":"1"});
            var Q1;
            Q1=makeQuery(id+"F22.opPattern","COPY",EDGE,{"derivedFrom":makeQuery(id+"F1.opExtrude","CAP_EDGE",EDGE,{"disambiguationData":[OSD([sQuery(id+"F0.wireOp",EDGE,"E3")])],"isStart":true}),"instanceName":"1"});
            transform(context, id + "F29", {"entities" : qUnion([Q0]), "transformType" : TransformType.ROTATION, "transformAxis" : qUnion([Q1]), "angle" : 42 * degree, "makeCopy" : false});
        }
        {
            var Q0;
            Q0=makeQuery(id+"F6.opExtrude","SWEPT_BODY",BODY,{"disambiguationData":[OSD([sQuery(id+"F0.wireOp",EDGE,"E23"),sQuery(id+"F0.wireOp",EDGE,"E33.MirrorCS"),sQuery(id+"F0.wireOp",EDGE,"E34.MirrorCS")])]});
            var Q1;
            Q1=makeQuery(id+"F4.opExtrude","SWEPT_BODY",BODY,{"disambiguationData":[OSD([sQuery(id+"F0.wireOp",EDGE,"E9"),sQuery(id+"F0.wireOp",EDGE,"E23"),sQuery(id+"F0.wireOp",EDGE,"E24")])]});
            var Q2;
            Q2=makeQuery(id+"F3.opExtrude","SWEPT_BODY",BODY,{"disambiguationData":[OSD([sQuery(id+"F0.wireOp",EDGE,"E14"),sQuery(id+"F0.wireOp",EDGE,"E25"),sQuery(id+"F0.wireOp",EDGE,"E26")])]});
            var Q3;
            Q3=makeQuery(id+"F5.opExtrude","SWEPT_BODY",BODY,{"disambiguationData":[OSD([sQuery(id+"F0.wireOp",EDGE,"E26"),sQuery(id+"F0.wireOp",EDGE,"E35"),sQuery(id+"F0.wireOp",EDGE,"E36")])]});
            var Q4;
            Q4=makeQuery(id+"F6.opExtrude","SWEPT_BODY",BODY,{"disambiguationData":[OSD([sQuery(id+"F0.wireOp",EDGE,"E20"),sQuery(id+"F0.wireOp",EDGE,"E29.MirrorCS"),sQuery(id+"F0.wireOp",EDGE,"E30.MirrorCS")])]});
            var Q5;
            Q5=makeQuery(id+"F4.opExtrude","SWEPT_BODY",BODY,{"disambiguationData":[OSD([sQuery(id+"F0.wireOp",EDGE,"E12"),sQuery(id+"F0.wireOp",EDGE,"E19"),sQuery(id+"F0.wireOp",EDGE,"E20")])]});
            deleteBodies(context, id + "F30", {"entities" : qUnion([Q0, Q1, Q2, Q3, Q4, Q5])});
        }
        {
            var Q0;
            Q0=makeQuery(id+"F3.opExtrude","SWEPT_BODY",BODY,{"disambiguationData":[OSD([sQuery(id+"F0.wireOp",EDGE,"E11"),sQuery(id+"F0.wireOp",EDGE,"E17"),sQuery(id+"F0.wireOp",EDGE,"E18")])]});
            var Q1;
            Q1=makeQuery(id+"F5.opExtrude","SWEPT_BODY",BODY,{"disambiguationData":[OSD([sQuery(id+"F0.wireOp",EDGE,"E18"),sQuery(id+"F0.wireOp",EDGE,"E27"),sQuery(id+"F0.wireOp",EDGE,"E28")])]});
            deleteBodies(context, id + "F31", {"entities" : qUnion([Q0, Q1])});
        }
        {
            var Q0;
            Q0=makeQuery(id+"F22.opPattern","COPY",BODY,{"derivedFrom":makeQuery(id+"F3.opExtrude","SWEPT_BODY",BODY,{"disambiguationData":[OSD([sQuery(id+"F0.wireOp",EDGE,"E11"),sQuery(id+"F0.wireOp",EDGE,"E17"),sQuery(id+"F0.wireOp",EDGE,"E18")])]}),"instanceName":"1"});
            var Q1;
            Q1=makeQuery(id+"F22.opPattern","COPY",BODY,{"derivedFrom":makeQuery(id+"F5.opExtrude","SWEPT_BODY",BODY,{"disambiguationData":[OSD([sQuery(id+"F0.wireOp",EDGE,"E18"),sQuery(id+"F0.wireOp",EDGE,"E27"),sQuery(id+"F0.wireOp",EDGE,"E28")])]}),"instanceName":"1"});
            var Q2;
            Q2=makeQuery(id+"F22.opPattern","COPY",BODY,{"derivedFrom":makeQuery(id+"F6.opExtrude","SWEPT_BODY",BODY,{"disambiguationData":[OSD([sQuery(id+"F0.wireOp",EDGE,"E23"),sQuery(id+"F0.wireOp",EDGE,"E33.MirrorCS"),sQuery(id+"F0.wireOp",EDGE,"E34.MirrorCS")])]}),"instanceName":"1"});
            var Q3;
            Q3=makeQuery(id+"F22.opPattern","COPY",BODY,{"derivedFrom":makeQuery(id+"F4.opExtrude","SWEPT_BODY",BODY,{"disambiguationData":[OSD([sQuery(id+"F0.wireOp",EDGE,"E9"),sQuery(id+"F0.wireOp",EDGE,"E23"),sQuery(id+"F0.wireOp",EDGE,"E24")])]}),"instanceName":"1"});
            var Q4;
            Q4=makeQuery(id+"F22.opPattern","COPY",BODY,{"derivedFrom":makeQuery(id+"F3.opExtrude","SWEPT_BODY",BODY,{"disambiguationData":[OSD([sQuery(id+"F0.wireOp",EDGE,"E14"),sQuery(id+"F0.wireOp",EDGE,"E25"),sQuery(id+"F0.wireOp",EDGE,"E26")])]}),"instanceName":"1"});
            var Q5;
            Q5=makeQuery(id+"F22.opPattern","COPY",BODY,{"derivedFrom":makeQuery(id+"F5.opExtrude","SWEPT_BODY",BODY,{"disambiguationData":[OSD([sQuery(id+"F0.wireOp",EDGE,"E26"),sQuery(id+"F0.wireOp",EDGE,"E35"),sQuery(id+"F0.wireOp",EDGE,"E36")])]}),"instanceName":"1"});
            var Q6;
            Q6=makeQuery(id+"F22.opPattern","COPY",BODY,{"derivedFrom":makeQuery(id+"F4.opExtrude","SWEPT_BODY",BODY,{"disambiguationData":[OSD([sQuery(id+"F0.wireOp",EDGE,"E12"),sQuery(id+"F0.wireOp",EDGE,"E19"),sQuery(id+"F0.wireOp",EDGE,"E20")])]}),"instanceName":"1"});
            var Q7;
            Q7=makeQuery(id+"F22.opPattern","COPY",BODY,{"derivedFrom":makeQuery(id+"F6.opExtrude","SWEPT_BODY",BODY,{"disambiguationData":[OSD([sQuery(id+"F0.wireOp",EDGE,"E20"),sQuery(id+"F0.wireOp",EDGE,"E29.MirrorCS"),sQuery(id+"F0.wireOp",EDGE,"E30.MirrorCS")])]}),"instanceName":"1"});
            deleteBodies(context, id + "F32", {"entities" : qUnion([Q0, Q1, Q2, Q3, Q4, Q5, Q6, Q7])});
        }
        {
            var Q0;
            Q0=makeQuery(id+"F22.opPattern","COPY",BODY,{"derivedFrom":makeQuery(id+"F1.opExtrude","SWEPT_BODY",BODY,{"disambiguationData":[OSD([sQuery(id+"F0.wireOp",EDGE,"E5"),sQuery(id+"F0.wireOp",EDGE,"E8"),sQuery(id+"F0.wireOp",EDGE,"E14")])]}),"instanceName":"1"});
            var Q1;
            Q1=makeQuery(id+"F22.opPattern","COPY",BODY,{"derivedFrom":makeQuery(id+"F2.opExtrude","SWEPT_BODY",BODY,{"disambiguationData":[OSD([sQuery(id+"F0.wireOp",EDGE,"E4"),sQuery(id+"F0.wireOp",EDGE,"E7"),sQuery(id+"F0.wireOp",EDGE,"E9")])]}),"instanceName":"1"});
            var Q2;
            Q2=makeQuery(id+"F22.opPattern","COPY",BODY,{"derivedFrom":makeQuery(id+"F2.opExtrude","SWEPT_BODY",BODY,{"disambiguationData":[OSD([sQuery(id+"F0.wireOp",EDGE,"E2"),sQuery(id+"F0.wireOp",EDGE,"E8"),sQuery(id+"F0.wireOp",EDGE,"E13")])]}),"instanceName":"1"});
            var Q3;
            Q3=makeQuery(id+"F1.opExtrude","SWEPT_BODY",BODY,{"disambiguationData":[OSD([sQuery(id+"F0.wireOp",EDGE,"E5"),sQuery(id+"F0.wireOp",EDGE,"E8"),sQuery(id+"F0.wireOp",EDGE,"E14")])]});
            var Q4;
            Q4=makeQuery(id+"F2.opExtrude","SWEPT_BODY",BODY,{"disambiguationData":[OSD([sQuery(id+"F0.wireOp",EDGE,"E4"),sQuery(id+"F0.wireOp",EDGE,"E7"),sQuery(id+"F0.wireOp",EDGE,"E9")])]});
            var Q5;
            Q5=makeQuery(id+"F1.opExtrude","SWEPT_BODY",BODY,{"disambiguationData":[OSD([sQuery(id+"F0.wireOp",EDGE,"E3"),sQuery(id+"F0.wireOp",EDGE,"E7"),sQuery(id+"F0.wireOp",EDGE,"E10")])]});
            deleteBodies(context, id + "F33", {"entities" : qUnion([Q0, Q1, Q2, Q3, Q4, Q5])});
        }
        {
            var Q0;
            Q0=qCreatedBy(makeId("Right.planeOp"),FACE);
            cPlane(context, id + "F34", {"entities" : qUnion([Q0]), "cplaneType" : CPlaneType.OFFSET, "offset" : 76.2 * mm, "width" : 152.4 * mm, "height" : 152.4 * mm});
        }
        {
            var Q0;
            Q0=qCreatedBy(id+"F26.planeOp",FACE);
            var sketch = newSketch(context, id + "F35", { "sketchPlane" : qUnion([Q0])});
            skPoint(sketch, "E48", {"position": v(76.2, -43.62) * mm});
            skPoint(sketch, "E49", {"position": v(76.2, 0) * mm});
            skLineSegment(sketch, "E50", {"start": v(76.2, 0) * mm, "end": v(76.2, -43.62) * mm});
            skSolve(sketch);
        }
    });
